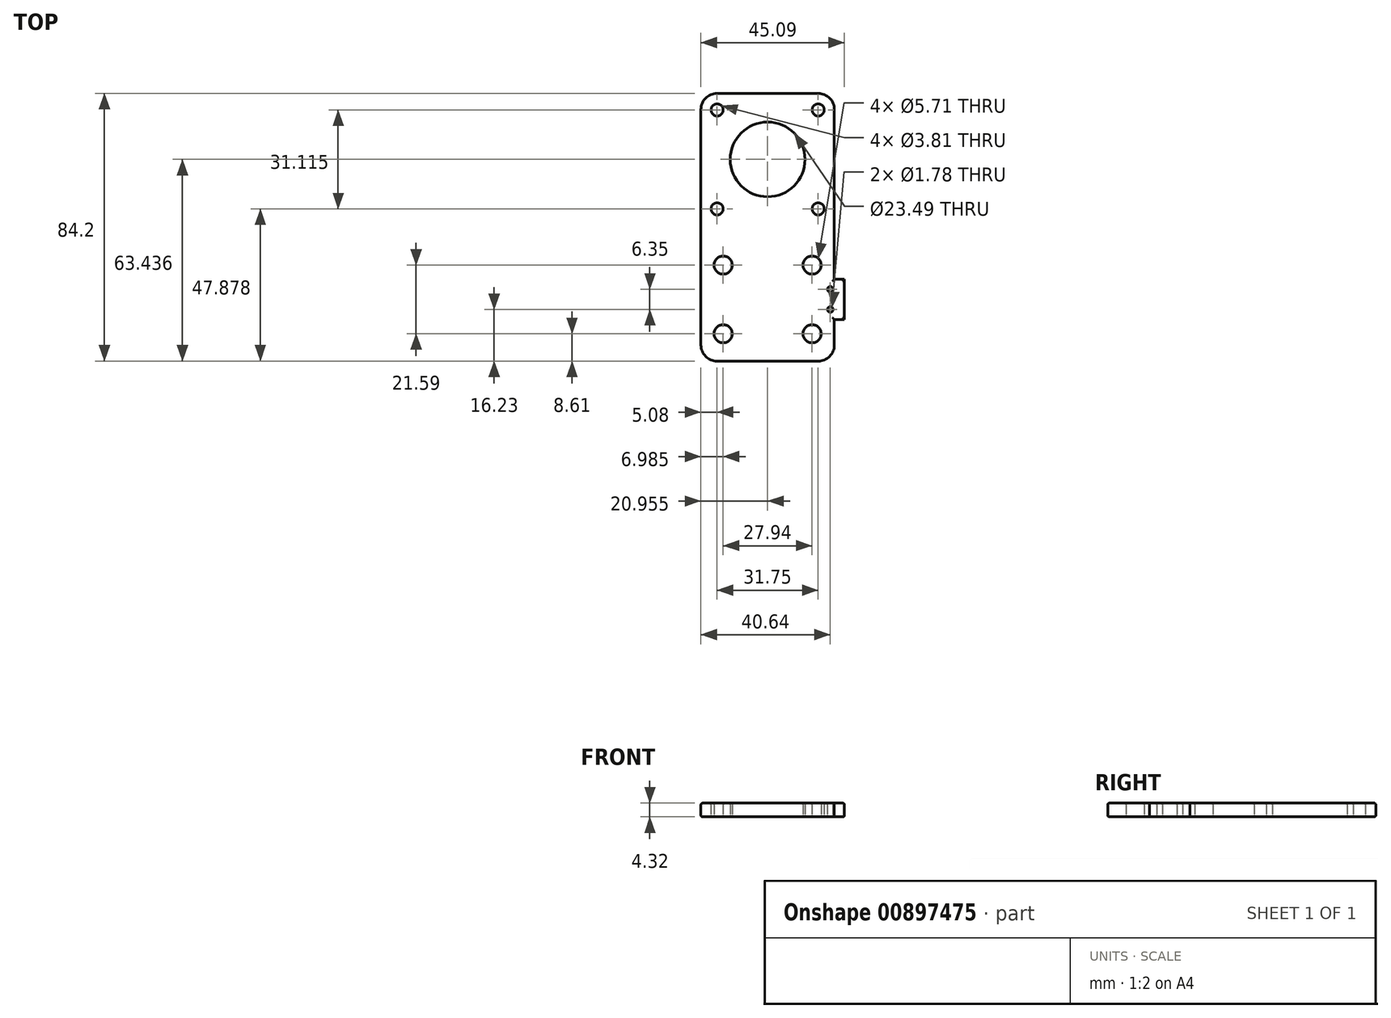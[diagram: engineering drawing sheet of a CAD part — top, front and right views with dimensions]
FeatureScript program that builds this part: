
annotation { "Feature Type Name" : "Feature", "Feature Type Description" : "" }
export const myFeature = defineFeature(function(context is Context, id is Id, definition is map)
    precondition{}
    {
        {
            var Q0;
            Q0=qCreatedBy(makeId("Top.planeOp"),FACE);
            var sketch = newSketch(context, id + "F0", { "sketchPlane" : qUnion([Q0])});
            skLineSegment(sketch, "E0", {"start": v(0, 0) * mm, "end": v(0, 63.5) * mm});
            skLineSegment(sketch, "E1", {"start": v(0, 63.5) * mm, "end": v(-41.91, 63.5) * mm});
            skLineSegment(sketch, "E2", {"start": v(-41.91, 63.5) * mm, "end": v(-41.91, 19) * mm});
            skLineSegment(sketch, "E3", {"start": v(-41.91, 19) * mm, "end": v(-41.91, 19) * mm});
            skLineSegment(sketch, "E4", {"start": v(-41.91, 19) * mm, "end": v(-41.91, 0) * mm});
            skCircle(sketch, "E5", {"center": v(-20.96, 42.74) * mm, "radius": 11.75 * mm});
            skCircle(sketch, "E6", {"center": v(-34.92, 9.5) * mm, "radius": 2.86 * mm});
            skLineSegment(sketch, "E7.top", {"start": v(-41.91, -20.7) * mm, "end": v(0, -20.7) * mm});
            skLineSegment(sketch, "E7.left", {"start": v(-41.91, 0) * mm, "end": v(-41.91, -20.7) * mm});
            skLineSegment(sketch, "E7.right", {"start": v(0, 0) * mm, "end": v(0, -20.7) * mm});
            skCircle(sketch, "E8", {"center": v(-34.92, -12.1) * mm, "radius": 2.86 * mm});
            skLineSegment(sketch, "E9", {"start": v(-41.91, 9.5) * mm, "end": v(-34.92, 9.5) * mm, "construction": true});
            skLineSegment(sketch, "E10", {"start": v(-20.96, 63.5) * mm, "end": v(-20.95, -20.7) * mm, "construction": true});
            skCircle(sketch, "E11", {"center": v(-36.83, 58.3) * mm, "radius": 1.9 * mm});
            skCircle(sketch, "E12", {"center": v(-5.08, 58.3) * mm, "radius": 1.9 * mm});
            skCircle(sketch, "E13", {"center": v(-5.08, 27.18) * mm, "radius": 1.9 * mm});
            skCircle(sketch, "E14", {"center": v(-36.83, 27.18) * mm, "radius": 1.9 * mm});
            skCircle(sketch, "E15", {"center": v(-6.99, -12.1) * mm, "radius": 2.86 * mm});
            skCircle(sketch, "E16", {"center": v(-6.99, 9.5) * mm, "radius": 2.86 * mm});
            skLineSegment(sketch, "E17", {"start": v(-36.83, 58.3) * mm, "end": v(-36.83, 27.18) * mm, "construction": true});
            skLineSegment(sketch, "E18", {"start": v(-36.83, 42.74) * mm, "end": v(-20.96, 42.74) * mm, "construction": true});
            skCircle(sketch, "E19", {"center": v(-1.27, 1.88) * mm, "radius": 0.89 * mm});
            skCircle(sketch, "E20", {"center": v(-1.27, -4.47) * mm, "radius": 0.89 * mm});
            skLineSegment(sketch, "E21", {"start": v(-6.99, 9.5) * mm, "end": v(-6.99, -12.1) * mm, "construction": true});
            skLineSegment(sketch, "E22", {"start": v(-1.27, 1.88) * mm, "end": v(-1.27, -4.47) * mm, "construction": true});
            skLineSegment(sketch, "E23", {"start": v(-1.27, -1.3) * mm, "end": v(-6.99, -1.3) * mm, "construction": true});
            skSolve(sketch);
        }
        {
            var Q0;
            Q0=makeQuery(id+"F0.imprint","IMPRINT",FACE,{"disambiguationData":[TD([[makeQuery(id+"F0.imprint","IMPRINT",EDGE,{"derivedFrom":sQuery(id+"F0.wireOp",EDGE,"E0")}),1.0]])]});
            var Q1;
            Q1=makeQuery(id+"F0.imprint","IMPRINT",FACE,{"disambiguationData":[TD([[makeQuery(id+"F0.imprint","IMPRINT",EDGE,{"derivedFrom":sQuery(id+"F0.wireOp",EDGE,"E7.bottom")}),-1.0]])]});
            extrude(context, id + "F1", {"entities" : qUnion([Q0, Q1]), "depth" : 4.32 * mm, "offsetDistance" : 25.4 * mm});
        }
        {
            var Q0;
            Q0=makeQuery(id+"F1.opExtrude","SWEPT_FACE",FACE,{"disambiguationData":[OSD([sQuery(id+"F0.wireOp",EDGE,"E0"),sQuery(id+"F0.wireOp",EDGE,"E7.right")])]});
            var sketch = newSketch(context, id + "F2", { "sketchPlane" : qUnion([Q0])});
            skLineSegment(sketch, "E24.bottom", {"start": v(-7.62, 4.32) * mm, "end": v(5.08, 4.32) * mm});
            skLineSegment(sketch, "E24.top", {"start": v(-7.62, 0) * mm, "end": v(5.08, 0) * mm});
            skLineSegment(sketch, "E24.left", {"start": v(-7.62, 4.32) * mm, "end": v(-7.62, 0) * mm});
            skLineSegment(sketch, "E24.right", {"start": v(5.08, 4.32) * mm, "end": v(5.08, 0) * mm});
            skSolve(sketch);
        }
        {
            var Q0;
            Q0 = qSketchRegion(id + "F2", true);
            extrude(context, id + "F3", {"entities" : qUnion([Q0]), "operationType" : NewBodyOperationType.ADD, "depth" : 3.17 * mm, "offsetDistance" : 25.4 * mm});
        }
        {
            var Q0;
            Q0=makeQuery(id+"F1.opExtrude","SWEPT_EDGE",EDGE,{"disambiguationData":[OSD([sQuery(id+"F0.wireOp",EDGE,"E0"),sQuery(id+"F0.wireOp",EDGE,"jd0ScVzn-dBjU-jrx6-kBj3-BUJqmgKr12Eg")])]});
            var Q1;
            Q1=makeQuery(id+"F1.opExtrude","SWEPT_EDGE",EDGE,{"disambiguationData":[OSD([sQuery(id+"F0.wireOp",EDGE,"E4"),sQuery(id+"F0.wireOp",EDGE,"jd0ScVzn-dBjU-jrx6-kBj3-BUJqmgKr12Eg")])]});
            var Q2;
            Q2=makeQuery(id+"F1.opExtrude","SWEPT_EDGE",EDGE,{"disambiguationData":[OSD([sQuery(id+"F0.wireOp",EDGE,"E3"),sQuery(id+"F0.wireOp",EDGE,"E4")])]});
            var Q3;
            Q3=makeQuery(id+"F1.opExtrude","SWEPT_EDGE",EDGE,{"disambiguationData":[OSD([sQuery(id+"F0.wireOp",EDGE,"E2"),sQuery(id+"F0.wireOp",EDGE,"E3")])]});
            var Q4;
            Q4=makeQuery(id+"F1.opExtrude","SWEPT_EDGE",EDGE,{"disambiguationData":[OSD([sQuery(id+"F0.wireOp",EDGE,"E1"),sQuery(id+"F0.wireOp",EDGE,"E2")])]});
            var Q5;
            Q5=makeQuery(id+"F1.opExtrude","SWEPT_EDGE",EDGE,{"disambiguationData":[OSD([sQuery(id+"F0.wireOp",EDGE,"E0"),sQuery(id+"F0.wireOp",EDGE,"E1")])]});
            var Q6;
            Q6=makeQuery(id+"F1.opExtrude","SWEPT_EDGE",EDGE,{"disambiguationData":[OSD([sQuery(id+"F0.wireOp",EDGE,"E7.top"),sQuery(id+"F0.wireOp",EDGE,"E7.right")])]});
            var Q7;
            Q7=makeQuery(id+"F1.opExtrude","SWEPT_EDGE",EDGE,{"disambiguationData":[OSD([sQuery(id+"F0.wireOp",EDGE,"E7.top"),sQuery(id+"F0.wireOp",EDGE,"E7.left")])]});
            fillet(context, id + "F4", {"entities" : qUnion([Q0, Q1, Q2, Q3, Q4, Q5, Q6, Q7]), "radius" : 5.08 * mm, "tangentPropagation" : true, "allowEdgeOverflow" : false});
        }
        {
            var Q0;
            Q0=makeQuery(id+"F1.opExtrude","CAP_EDGE",EDGE,{"disambiguationData":[OSD([sQuery(id+"F0.wireOp",EDGE,"E0")])],"isStart":false});
            var Q1;
            Q1=makeQuery(id+"F1.opExtrude","CAP_EDGE",EDGE,{"disambiguationData":[OSD([sQuery(id+"F0.wireOp",EDGE,"E6")])],"isStart":false});
            var Q2;
            Q2=makeQuery(id+"F1.opExtrude","CAP_EDGE",EDGE,{"disambiguationData":[OSD([sQuery(id+"F0.wireOp",EDGE,"NaQKEjHk-Z6LA-96tM-WqRa-bFAFSZEO5QkA")])],"isStart":false});
            var Q3;
            Q3=makeQuery(id+"F1.opExtrude","CAP_EDGE",EDGE,{"disambiguationData":[OSD([sQuery(id+"F0.wireOp",EDGE,"E5")])],"isStart":false});
            var Q4;
            Q4=makeQuery(id+"F1.opExtrude","CAP_EDGE",EDGE,{"disambiguationData":[OSD([sQuery(id+"F0.wireOp",EDGE,"E0")])],"isStart":true});
            var Q5;
            Q5=makeQuery(id+"F1.opExtrude","CAP_EDGE",EDGE,{"disambiguationData":[OSD([sQuery(id+"F0.wireOp",EDGE,"E6")])],"isStart":true});
            var Q6;
            Q6=makeQuery(id+"F1.opExtrude","CAP_EDGE",EDGE,{"disambiguationData":[OSD([sQuery(id+"F0.wireOp",EDGE,"NaQKEjHk-Z6LA-96tM-WqRa-bFAFSZEO5QkA")])],"isStart":true});
            var Q7;
            Q7=makeQuery(id+"F1.opExtrude","CAP_EDGE",EDGE,{"disambiguationData":[OSD([sQuery(id+"F0.wireOp",EDGE,"E8")])],"isStart":false});
            var Q8;
            Q8=makeQuery(id+"F1.opExtrude","CAP_EDGE",EDGE,{"disambiguationData":[OSD([sQuery(id+"F0.wireOp",EDGE,"E8")])],"isStart":true});
            var Q9;
            Q9=makeQuery(id+"F1.opExtrude","CAP_EDGE",EDGE,{"disambiguationData":[OSD([sQuery(id+"F0.wireOp",EDGE,"E5")])],"isStart":true});
            var Q10;
            Q10=makeQuery(id+"F1.opExtrude","CAP_FACE",FACE,{"disambiguationData":[OSD([sQuery(id+"F0.wireOp",EDGE,"E0"),sQuery(id+"F0.wireOp",EDGE,"E1"),sQuery(id+"F0.wireOp",EDGE,"E2"),sQuery(id+"F0.wireOp",EDGE,"E4"),sQuery(id+"F0.wireOp",EDGE,"E5"),sQuery(id+"F0.wireOp",EDGE,"E6"),sQuery(id+"F0.wireOp",EDGE,"E7.top"),sQuery(id+"F0.wireOp",EDGE,"E7.left"),sQuery(id+"F0.wireOp",EDGE,"E7.right"),sQuery(id+"F0.wireOp",EDGE,"E8"),sQuery(id+"F0.wireOp",EDGE,"E11"),sQuery(id+"F0.wireOp",EDGE,"E12"),sQuery(id+"F0.wireOp",EDGE,"E13"),sQuery(id+"F0.wireOp",EDGE,"E14"),sQuery(id+"F0.wireOp",EDGE,"E15"),sQuery(id+"F0.wireOp",EDGE,"E16")])],"isStart":false});
            var Q11;
            Q11=makeQuery(id+"F1.opExtrude","CAP_FACE",FACE,{"disambiguationData":[OSD([sQuery(id+"F0.wireOp",EDGE,"E0"),sQuery(id+"F0.wireOp",EDGE,"E1"),sQuery(id+"F0.wireOp",EDGE,"E2"),sQuery(id+"F0.wireOp",EDGE,"E4"),sQuery(id+"F0.wireOp",EDGE,"E5"),sQuery(id+"F0.wireOp",EDGE,"E6"),sQuery(id+"F0.wireOp",EDGE,"E7.top"),sQuery(id+"F0.wireOp",EDGE,"E7.left"),sQuery(id+"F0.wireOp",EDGE,"E7.right"),sQuery(id+"F0.wireOp",EDGE,"E8"),sQuery(id+"F0.wireOp",EDGE,"E11"),sQuery(id+"F0.wireOp",EDGE,"E12"),sQuery(id+"F0.wireOp",EDGE,"E13"),sQuery(id+"F0.wireOp",EDGE,"E14"),sQuery(id+"F0.wireOp",EDGE,"E15"),sQuery(id+"F0.wireOp",EDGE,"E16")])],"isStart":true});
            fillet(context, id + "F5", {"entities" : qUnion([Q0, Q1, Q2, Q3, Q4, Q5, Q6, Q7, Q8, Q9, Q10, Q11]), "radius" : 0.5 * mm, "tangentPropagation" : true, "allowEdgeOverflow" : false});
        }
    });
